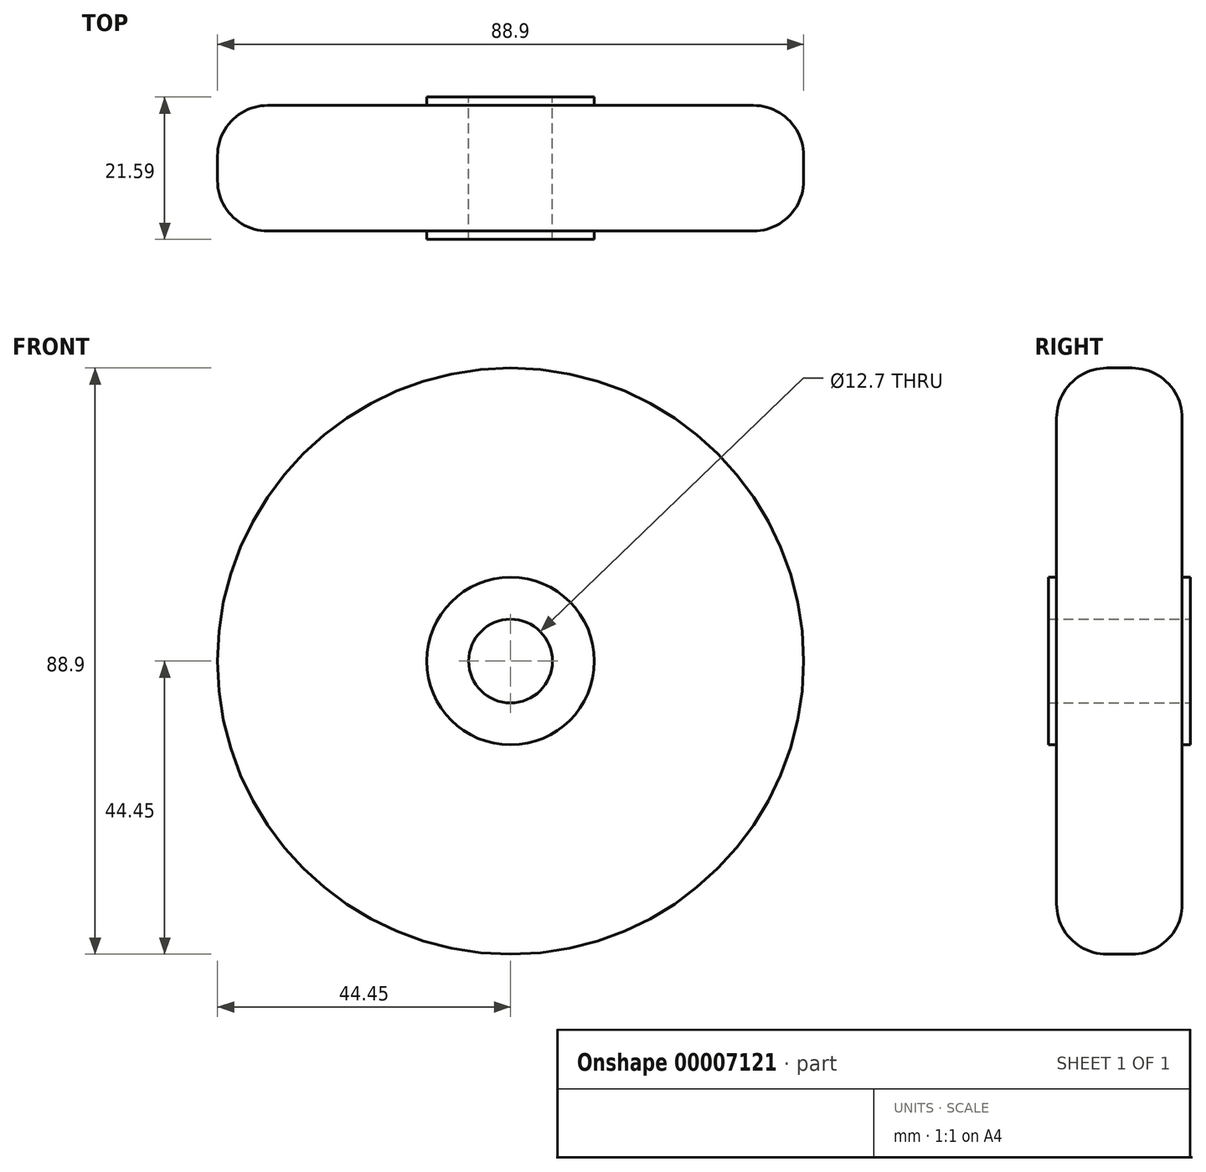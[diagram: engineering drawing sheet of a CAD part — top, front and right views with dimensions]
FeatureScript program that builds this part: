
annotation { "Feature Type Name" : "Feature", "Feature Type Description" : "" }
export const myFeature = defineFeature(function(context is Context, id is Id, definition is map)
    precondition{}
    {
        {
            var Q0;
            Q0=qCreatedBy(makeId("Front.planeOp"),FACE);
            var sketch = newSketch(context, id + "F0", { "sketchPlane" : qUnion([Q0])});
            skCircle(sketch, "E0", {"center": v(0, 0) * mm, "radius": 6.35 * mm});
            skCircle(sketch, "E1", {"center": v(0, 0) * mm, "radius": 12.7 * mm});
            skCircle(sketch, "E2", {"center": v(0, 0) * mm, "radius": 44.45 * mm});
            skSolve(sketch);
        }
        {
            var Q0;
            Q0=makeQuery(id+"F0.imprint","IMPRINT",FACE,{"disambiguationData":[TD([[makeQuery(id+"F0.imprint","IMPRINT",EDGE,{"derivedFrom":sQuery(id+"F0.wireOp",EDGE,"E1")}),-1.0]])]});
            extrude(context, id + "F1", {"entities" : qUnion([Q0]), "depth" : 19.05 * mm});
        }
        {
            var Q0;
            Q0=makeQuery(id+"F0.imprint","IMPRINT",FACE,{"disambiguationData":[TD([[makeQuery(id+"F0.imprint","IMPRINT",EDGE,{"derivedFrom":sQuery(id+"F0.wireOp",EDGE,"E0")}),-1.0]])]});
            extrude(context, id + "F2", {"entities" : qUnion([Q0]), "operationType" : NewBodyOperationType.ADD, "depth" : 20.32 * mm});
        }
        {
            var Q0;
            Q0=makeQuery(id+"F0.imprint","IMPRINT",FACE,{"disambiguationData":[TD([[makeQuery(id+"F0.imprint","IMPRINT",EDGE,{"derivedFrom":sQuery(id+"F0.wireOp",EDGE,"E0")}),-1.0]])]});
            extrude(context, id + "F3", {"entities" : qUnion([Q0]), "operationType" : NewBodyOperationType.ADD, "oppositeDirection" : true, "depth" : 1.27 * mm});
        }
        {
            var Q0;
            Q0=makeQuery(id+"F1.opExtrude","CAP_EDGE",EDGE,{"disambiguationData":[OSD([sQuery(id+"F0.wireOp",EDGE,"E2")])],"isStart":true});
            var Q1;
            Q1=makeQuery(id+"F1.opExtrude","CAP_EDGE",EDGE,{"disambiguationData":[OSD([sQuery(id+"F0.wireOp",EDGE,"E2")])],"isStart":false});
            fillet(context, id + "F4", {"entities" : qUnion([Q0, Q1]), "radius" : 7.62 * mm, "tangentPropagation" : true, "allowEdgeOverflow" : false});
        }
    });
